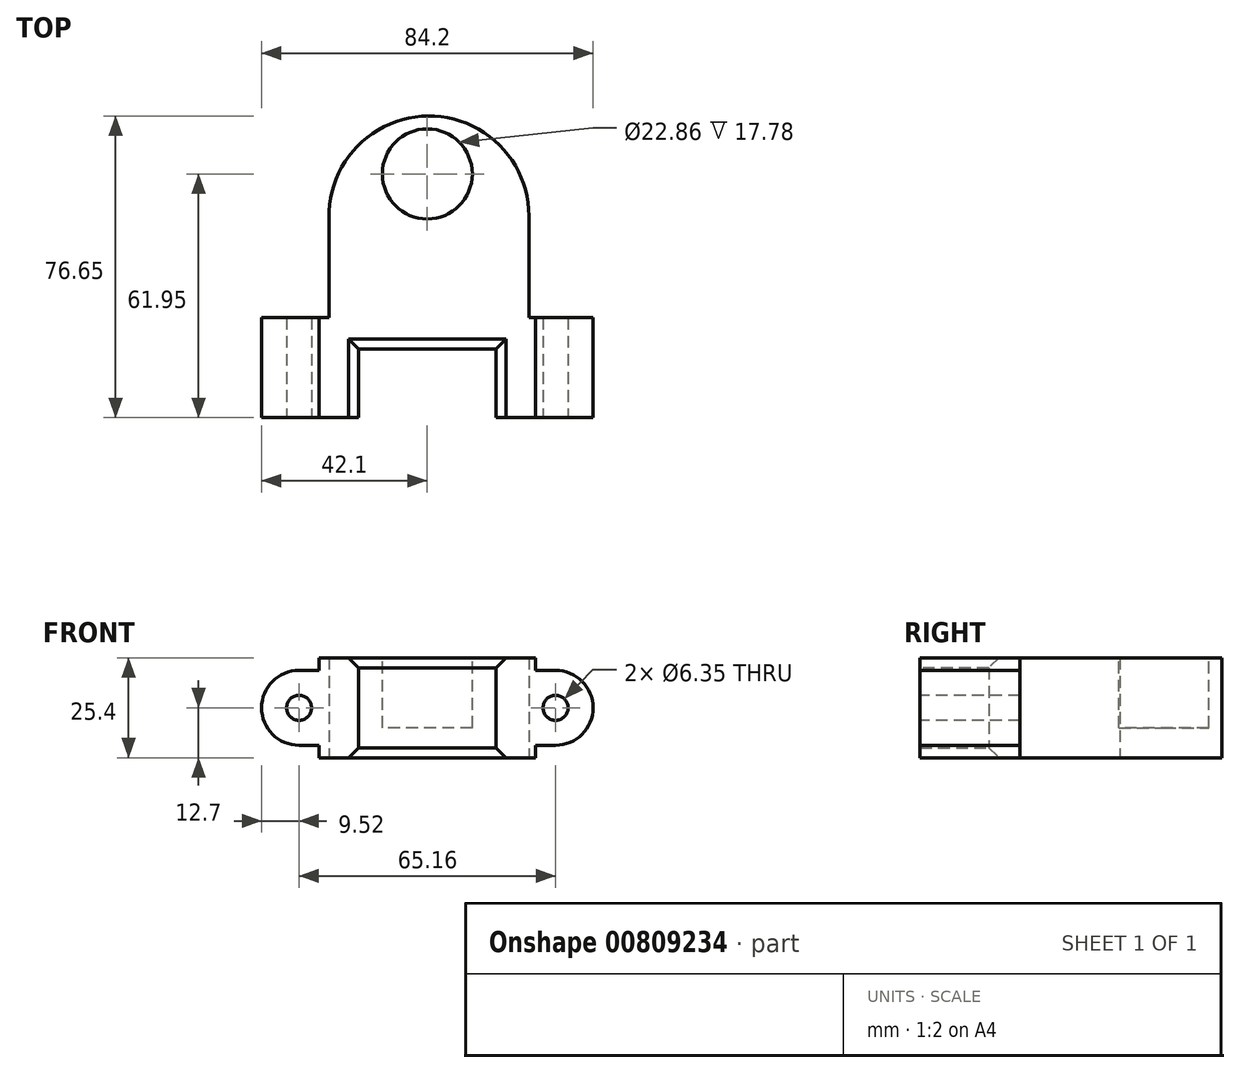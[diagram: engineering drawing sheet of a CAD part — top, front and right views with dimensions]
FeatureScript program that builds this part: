
annotation { "Feature Type Name" : "Feature", "Feature Type Description" : "" }
export const myFeature = defineFeature(function(context is Context, id is Id, definition is map)
    precondition{}
    {
        {
            var Q0;
            Q0=qCreatedBy(makeId("Top.planeOp"),FACE);
            var sketch = newSketch(context, id + "F0", { "sketchPlane" : qUnion([Q0])});
            skLineSegment(sketch, "E0.top", {"start": v(17.5, 17.5) * mm, "end": v(-17.5, 17.5) * mm});
            skLineSegment(sketch, "E0.left", {"start": v(17.5, 0) * mm, "end": v(17.5, 17.5) * mm});
            skLineSegment(sketch, "E0.right", {"start": v(-17.5, 0) * mm, "end": v(-17.5, 17.5) * mm});
            skPoint(sketch, "E0.middle", {"position": v(0, 0) * mm});
            skLineSegment(sketch, "E1.top", {"start": v(27.5, 25.4) * mm, "end": v(-27.5, 25.4) * mm});
            skLineSegment(sketch, "E1.left", {"start": v(27.5, 0) * mm, "end": v(27.5, 25.4) * mm});
            skLineSegment(sketch, "E1.right", {"start": v(-27.5, 0) * mm, "end": v(-27.5, 25.4) * mm});
            skLineSegment(sketch, "E2", {"start": v(-27.5, 0) * mm, "end": v(27.5, 0) * mm});
            skLineSegment(sketch, "E3", {"start": v(-24.96, 25.4) * mm, "end": v(-24.96, 50.8) * mm});
            skLineSegment(sketch, "E4", {"start": v(25.84, 25.4) * mm, "end": v(25.84, 51.25) * mm});
            skArc(sketch, "E5", {"start": v(25.84, 51.25) * mm, "mid": v(0.21, 76.65) * mm, "end": v(-24.96, 50.8) * mm});
            skSolve(sketch);
        }
        {
            var Q0;
            {var subQ0=sQuery(id+"F0.wireOp",EDGE,"E3");Q0=makeQuery(id+"F0.imprint","IMPRINT",FACE,{"disambiguationData":[TD([[makeQuery(id+"F0.imprint","IMPRINT",EDGE,{"derivedFrom":subQ0}),-1.0]])]});}
            var Q1;
            Q1=makeQuery(id+"F0.imprint","IMPRINT",FACE,{"disambiguationData":[TD([[makeQuery(id+"F0.imprint","IMPRINT",EDGE,{"derivedFrom":sQuery(id+"F0.wireOp",EDGE,"E0.top")}),-1.0]])]});
            extrude(context, id + "F1", {"entities" : qUnion([Q0, Q1]), "depth" : 25.4 * mm, "offsetDistance" : 25.4 * mm});
        }
        {
            var Q0;
            Q0=qCreatedBy(makeId("Front.planeOp"),FACE);
            var sketch = newSketch(context, id + "F2", { "sketchPlane" : qUnion([Q0])});
            skCircle(sketch, "E6", {"center": v(-32.58, 12.7) * mm, "radius": 3.18 * mm});
            skLineSegment(sketch, "E7", {"start": v(-27.5, 22.23) * mm, "end": v(-32.58, 22.23) * mm});
            skLineSegment(sketch, "E8", {"start": v(-27.5, 3.18) * mm, "end": v(-32.58, 3.18) * mm});
            skArc(sketch, "E9", {"start": v(-32.58, 22.23) * mm, "mid": v(-42.1, 12.7) * mm, "end": v(-32.58, 3.18) * mm});
            skLineSegment(sketch, "E10", {"start": v(-27.5, 22.23) * mm, "end": v(-27.5, 3.18) * mm});
            skSolve(sketch);
        }
        {
            var Q0;
            Q0=makeQuery(id+"F2.imprint","IMPRINT",FACE,{"disambiguationData":[TD([[makeQuery(id+"F2.imprint","IMPRINT",EDGE,{"derivedFrom":sQuery(id+"F2.wireOp",EDGE,"E6")}),-1.0]])]});
            extrude(context, id + "F3", {"entities" : qUnion([Q0]), "oppositeDirection" : true, "depth" : 25.4 * mm, "offsetDistance" : 25.4 * mm});
        }
        {
            var Q0;
            Q0=makeQuery(id+"F3.opExtrude","SWEPT_BODY",BODY,{"disambiguationData":[OSD([sQuery(id+"F2.wireOp",EDGE,"E6"),sQuery(id+"F2.wireOp",EDGE,"E7"),sQuery(id+"F2.wireOp",EDGE,"E8"),sQuery(id+"F2.wireOp",EDGE,"E9"),sQuery(id+"F2.wireOp",EDGE,"E10")])]});
            var Q1;
            Q1=qCreatedBy(makeId("Right.planeOp"),FACE);
            mirror(context, id + "F4", {"operationType" : NewBodyOperationType.ADD, "entities" : qUnion([Q0]), "mirrorPlane" : qUnion([Q1])});
        }
        {
            var Q0;
            Q0=makeQuery(id+"F1.opExtrude","CAP_FACE",FACE,{"disambiguationData":[OSD([sQuery(id+"F0.wireOp",EDGE,"E0.top"),sQuery(id+"F0.wireOp",EDGE,"E0.left"),sQuery(id+"F0.wireOp",EDGE,"E0.right"),sQuery(id+"F0.wireOp",EDGE,"E1.top"),sQuery(id+"F0.wireOp",EDGE,"E1.left"),sQuery(id+"F0.wireOp",EDGE,"E1.right"),sQuery(id+"F0.wireOp",EDGE,"E2"),sQuery(id+"F0.wireOp",EDGE,"mfYcxCVH-Ooqk-h47f-WzZS-GrRa9i6iQxS5")])],"isStart":false});
            var sketch = newSketch(context, id + "F5", { "sketchPlane" : qUnion([Q0])});
            skCircle(sketch, "E11", {"center": v(0, 61.95) * mm, "radius": 11.43 * mm});
            skSolve(sketch);
        }
        {
            var Q0;
            Q0=makeQuery(id+"F5.imprint","IMPRINT",FACE,{"disambiguationData":[TD([[makeQuery(id+"F5.imprint","IMPRINT",EDGE,{"derivedFrom":sQuery(id+"F5.wireOp",EDGE,"E11")}),1.0]])]});
            extrude(context, id + "F6", {"entities" : qUnion([Q0]), "operationType" : NewBodyOperationType.REMOVE, "oppositeDirection" : true, "depth" : 17.78 * mm, "offsetDistance" : 25.4 * mm});
        }
        {
            var Q0;
            Q0=makeQuery(id+"F1.opExtrude","CAP_EDGE",EDGE,{"disambiguationData":[OSD([sQuery(id+"F0.wireOp",EDGE,"E0.top")])],"isStart":false});
            var Q1;
            Q1=makeQuery(id+"F1.opExtrude","CAP_EDGE",EDGE,{"disambiguationData":[OSD([sQuery(id+"F0.wireOp",EDGE,"E0.left")])],"isStart":false});
            var Q2;
            Q2=makeQuery(id+"F1.opExtrude","CAP_EDGE",EDGE,{"disambiguationData":[OSD([sQuery(id+"F0.wireOp",EDGE,"E0.right")])],"isStart":false});
            var Q3;
            Q3=makeQuery(id+"F1.opExtrude","CAP_EDGE",EDGE,{"disambiguationData":[OSD([sQuery(id+"F0.wireOp",EDGE,"E0.left")])],"isStart":true});
            var Q4;
            Q4=makeQuery(id+"F1.opExtrude","CAP_EDGE",EDGE,{"disambiguationData":[OSD([sQuery(id+"F0.wireOp",EDGE,"E0.top")])],"isStart":true});
            var Q5;
            Q5=makeQuery(id+"F1.opExtrude","CAP_EDGE",EDGE,{"disambiguationData":[OSD([sQuery(id+"F0.wireOp",EDGE,"E0.right")])],"isStart":true});
            chamfer(context, id + "F7", {"entities" : qUnion([Q0, Q1, Q2, Q3, Q4, Q5]), "width" : 2.54 * mm, "tangentPropagation" : true});
        }
    });
